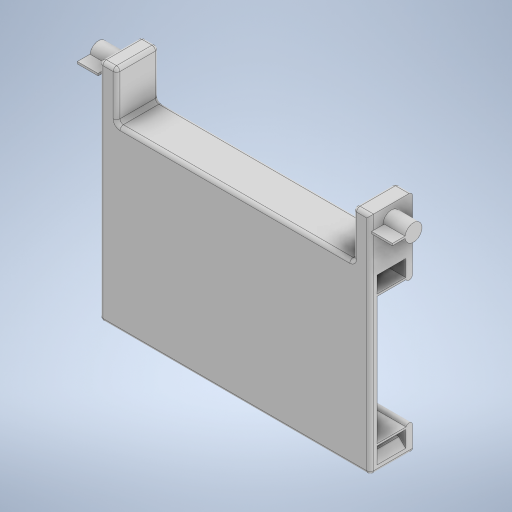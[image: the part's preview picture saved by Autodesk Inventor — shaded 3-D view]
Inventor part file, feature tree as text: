
AUTODESK INVENTOR PART (.ipt)
format: ipt  version: 2024 (Build 280153000, 153)  size: 409,088 bytes
history: native  units: mm
features: extrude x8, sketch x8, fillet x6, mirror x4, chamfer x1
ambient origin geometry x8: Origin, YZ Plane, XZ Plane, XY Plane, X Axis, Y Axis, Z Axis, Center Point
bodies: Volumenkörper1 (feature_tree)
feature tree (27):
  extrude  "Extrusion1"  Depth=5.2mm TaperAngle=0.0deg
  extrude  "Extrusion2"  Depth=37.7mm
  extrude  "Extrusion3"  Depth=1.0mm
  extrude  "Extrusion7"  Depth=2.0mm
  mirror  "Spiegeln2"
  extrude  "Extrusion8"  Depth=2.0mm
  extrude  "Extrusion9"  Depth=1.5mm
  mirror  "Spiegeln3"
  extrude  "Extrusion10"  Depth=0.3mm
  mirror  "Spiegeln4"
  extrude  "Extrusion11"  Depth=0.25mm TaperAngle=0.0deg
  mirror  "Spiegeln5"
  fillet  "Rundung1"  Radius=2.0mm
  fillet  "Rundung2"  Radius=2.5mm
  fillet  "Rundung3"  Radius=3.25mm
  fillet  "Rundung4"  Radius=0.3mm
  chamfer  "Fasen1"  Distance=0.4mm
  fillet  "Rundung5"  Radius=10.0mm
  fillet  "Rundung6"  Radius=0.3mm
  sketch  "Skizze1"  dims[d2=1.0mm d3=0.0mm d6=5.2mm d7=0.0mm]
  sketch  "Skizze2"  dims[d11=1.0mm d12=0.0mm d24=37.7mm]
  sketch  "Skizze3"  dims[d25=22.1mm d26=1.0mm]
  sketch  "Skizze7"  dims[d27=0.0mm d30=2.0mm]
  sketch  "Skizze8"  dims[d31=2.0mm d35=2.0mm]
  sketch  "Skizze9"  dims[d36=2.0mm d38=1.5mm]
  sketch  "Skizze11"  dims[d39=2.5mm d40=0.3mm d41=-8.726646mm]
  sketch  "Skizze12"  dims[d42=2.5mm d43=7.0mm d44=0.0mm d45=2.0mm d46=2.5mm d47=3.25mm d48=0.0mm d50=0.3mm d51=0.4mm d52=10.0mm d53=0.0mm d54=0.3mm d55=0.15mm d56=0.15mm d57=0.2mm d58=0.0mm d59=0.0mm d60=0.5mm d61=0.5mm d62=0.5mm d63=0.5mm d64=1.0mm d65=2.0mm d66=45.0deg d67=0.5mm d68=0.25mm d69=0.0mm d70=0.0mm d71=0.0mm]
